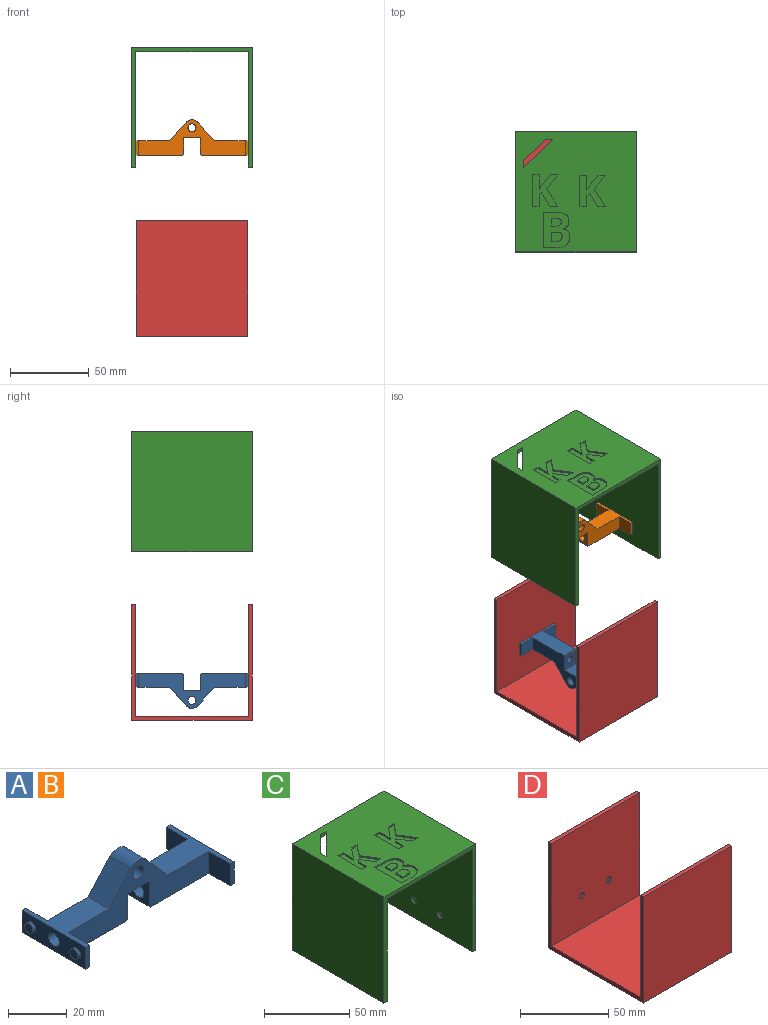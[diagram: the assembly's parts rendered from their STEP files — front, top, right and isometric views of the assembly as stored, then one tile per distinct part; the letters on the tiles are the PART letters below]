
ASSEMBLY  parts=4 mates=3
PART A: 35 faces, bbox 73.5x30.6x22.4 mm
  f0: plane 11.29x10.07mm, normal (0.75,0,0.67), area 151.4mm2, adj f1,f12,f13,f14
  f1: cylinder r=5.08mm len=10.01mm, axis (0,1,0), area 89.4mm2, adj f0,f2,f13,f14
  f2: plane 11.57x10.3mm, normal (-0.75,0,0.67), area 155mm2, adj f1,f3,f13,f14
  f3: plane 30.59x21.47mm, normal (0,0,1), area 252.2mm2, adj f2,f13,f14,f15,f16,f17,f18,f19
  f4: plane 30.59x29.85mm, normal (0,0,-1), area 336.1mm2, adj f5,f13,f14,f15,f16,f17,f18,f19
  f5: plane 10.01x0.64mm, normal (0.71,0,-0.71), area 9mm2, adj f4,f6,f13,f14
  f6: plane 10.3x10.01mm, normal (1,0,0), area 82.6mm2, adj f5,f7,f13,f14,f34
  f7: plane 10.16x10.01mm, normal (0,0,-1), area 101.7mm2, adj f6,f8,f13,f14
  f8: plane 10.3x10.01mm, normal (-1,0,0), area 82.6mm2, adj f7,f9,f13,f14,f33
  f9: plane 10.01x0.64mm, normal (-0.71,0,-0.71), area 9mm2, adj f8,f10,f13,f14
  f10: plane 30.59x29.85mm, normal (0,0,-1), area 336.1mm2, adj f9,f13,f14,f24,f25,f26,f27,f28
  f11: cylinder r=2.55mm len=10.01mm, axis (0,1,0), area 160.5mm2, adj f13,f14
  f12: plane 30.59x21.47mm, normal (0,0,1), area 252.2mm2, adj f0,f13,f14,f24,f25,f26,f27,f28
  f13: plane 67.49x22.39mm, normal (0,-1,0), area 699.3mm2, adj f0,f1,f2,f3,f4,f5,f6,f7
  f14: plane 67.49x22.39mm, normal (0,1,0), area 699.3mm2, adj f0,f1,f2,f3,f4,f5,f6,f7
  f15: plane 10.29x9.12mm, normal (1,0,0), area 93.9mm2, adj f3,f4,f13,f17
  f16: plane 9.12x1.82mm, normal (0,1,0), area 16.6mm2, adj f3,f4,f18,f19
  f17: plane 9.12x1.82mm, normal (0,-1,0), area 16.6mm2, adj f3,f4,f15,f18
  f18: plane 30.59x9.12mm, normal (-1,0,0), area 233.8mm2, adj f3,f4,f16,f17,f20,f22,f34
  f19: plane 10.29x9.12mm, normal (1,0,0), area 93.9mm2, adj f3,f4,f14,f16
  f20: cylinder r=1.98mm len=3.96mm, axis (1,0,0), area 14.9mm2, adj f18,f21
  f21: plane 3.96x3.96mm, normal (-1,0,0), area 12.3mm2, adj f20
  f22: cylinder r=1.98mm len=3.96mm, axis (1,0,0), area 14.9mm2, adj f18,f23
  f23: plane 3.96x3.96mm, normal (-1,0,0), area 12.3mm2, adj f22
  f24: plane 10.29x9.12mm, normal (-1,0,0), area 93.9mm2, adj f10,f12,f14,f25
  f25: plane 9.12x1.82mm, normal (0,1,0), area 16.6mm2, adj f10,f12,f24,f27
  f26: plane 9.12x1.82mm, normal (0,-1,0), area 16.6mm2, adj f10,f12,f27,f28
  f27: plane 30.59x9.12mm, normal (1,0,0), area 233.8mm2, adj f10,f12,f25,f26,f29,f31,f33
  f28: plane 10.29x9.12mm, normal (-1,0,0), area 93.9mm2, adj f10,f12,f13,f26
  f29: cylinder r=1.98mm len=3.96mm, axis (-1,0,0), area 14.9mm2, adj f27,f30
  f30: plane 3.96x3.96mm, normal (1,0,0), area 12.3mm2, adj f29
  f31: cylinder r=1.98mm len=3.96mm, axis (-1,0,0), area 14.9mm2, adj f27,f32
  f32: plane 3.96x3.96mm, normal (1,0,0), area 12.3mm2, adj f31
  f33: cylinder r=2.55mm len=30.48mm, axis (-1,0,0), area 488.9mm2, adj f8,f27
  f34: cylinder r=2.55mm len=30.48mm, axis (-1,0,0), area 488.9mm2, adj f6,f18
PART B: same geometry as A
PART C: 78 faces, bbox 76.2x76.2x76.2 mm
  f0: plane 76.2x76.2mm, normal (0,0,1), area 5029.8mm2, adj f3,f4,f6,f7,f10,f11,f12,f13
  f1: plane 76.2x71.12mm, normal (0,0,-1), area 5348.8mm2, adj f3,f4,f8,f9,f10,f11,f12,f13
  f2: plane 76.2x2.54mm, normal (0,0,-1), area 193.5mm2, adj f3,f4,f7,f9
  f3: plane 76.2x76.2mm, normal (0,-1,0), area 567.7mm2, adj f0,f1,f2,f5,f6,f7,f8,f9
  f4: plane 76.2x76.2mm, normal (0,1,0), area 567.7mm2, adj f0,f1,f2,f5,f6,f7,f8,f9
  f5: plane 76.2x2.54mm, normal (0,0,-1), area 193.5mm2, adj f3,f4,f6,f8
  f6: plane 76.2x76.2mm, normal (1,0,0), area 5806.4mm2, adj f0,f3,f4,f5
  f7: plane 76.2x76.2mm, normal (-1,0,0), area 5806.4mm2, adj f0,f2,f3,f4
  f8: plane 76.2x73.66mm, normal (-1,0,0), area 5586.6mm2, adj f1,f3,f4,f5,f75,f77
  f9: plane 76.2x73.66mm, normal (1,0,0), area 5586.6mm2, adj f1,f2,f3,f4,f71,f73
  f10: plane 4.49x2.54mm, normal (0,-1,0), area 11.4mm2, adj f0,f1,f11,f13
  f11: plane 13.47x13.47mm, normal (0.71,-0.71,0), area 48.4mm2, adj f0,f1,f10,f12
  f12: plane 4.49x2.54mm, normal (1,0,0), area 11.4mm2, adj f0,f1,f11,f13
  f13: plane 17.96x17.96mm, normal (-0.71,0.71,0), area 64.5mm2, adj f0,f1,f10,f12
  f14: plane 11.17x7.04mm, normal (-0.85,-0.53,0), area 13.4mm2, adj f0,f15,f26,f27
  f15: plane 8.87x6.99mm, normal (-0.79,0.62,0), area 11.5mm2, adj f0,f14,f16,f27
  f16: plane 4.72x1.02mm, normal (0,-1,0), area 4.8mm2, adj f0,f15,f17,f27
  f17: plane 6.81x5.43mm, normal (0.78,-0.62,0), area 8.9mm2, adj f0,f16,f18,f27
  f18: plane 2.36x1.67mm, normal (0.82,-0.58,0), area 2.9mm2, adj f0,f17,f19,f27
  f19: plane 9.17x1.02mm, normal (-1,0,0), area 9.3mm2, adj f0,f18,f20,f27
  f20: plane 4.25x1.02mm, normal (0,-1,0), area 4.3mm2, adj f0,f19,f21,f27
  f21: plane 20.04x1.02mm, normal (1,0,0), area 20.4mm2, adj f0,f20,f22,f27
  f22: plane 4.25x1.02mm, normal (0,1,0), area 4.3mm2, adj f0,f21,f23,f27
  f23: plane 7.15x1.02mm, normal (-1,0,0), area 7.3mm2, adj f0,f22,f24,f27
  f24: plane 1.79x1.29mm, normal (-0.58,0.81,0), area 2.2mm2, adj f0,f23,f25,f27
  f25: plane 8.44x5.25mm, normal (0.85,0.53,0), area 10.1mm2, adj f0,f24,f26,f27
  f26: plane 4.82x1.02mm, normal (0,1,0), area 4.9mm2, adj f0,f14,f25,f27
  f27: plane 20.04x16.12mm, normal (0,0,1), area 184.2mm2, adj f14,f15,f16,f17,f18,f19,f20,f21
  f28: plane 11.02x6.95mm, normal (-0.85,-0.53,0), area 13.2mm2, adj f0,f29,f40,f41
  f29: plane 8.75x6.9mm, normal (-0.79,0.62,0), area 11.3mm2, adj f0,f28,f30,f41
  f30: plane 4.65x1.02mm, normal (0,-1,0), area 4.7mm2, adj f0,f29,f31,f41
  f31: plane 6.72x5.36mm, normal (0.78,-0.62,0), area 8.7mm2, adj f0,f30,f32,f41
  f32: plane 2.33x1.65mm, normal (0.82,-0.58,0), area 2.9mm2, adj f0,f31,f33,f41
  f33: plane 9.05x1.02mm, normal (-1,0,0), area 9.2mm2, adj f0,f32,f34,f41
  f34: plane 4.19x1.02mm, normal (0,-1,0), area 4.3mm2, adj f0,f33,f35,f41
  f35: plane 19.76x1.02mm, normal (1,0,0), area 20.1mm2, adj f0,f34,f36,f41
  f36: plane 4.19x1.02mm, normal (0,1,0), area 4.3mm2, adj f0,f35,f37,f41
  f37: plane 7.06x1.02mm, normal (-1,0,0), area 7.2mm2, adj f0,f36,f38,f41
  f38: plane 1.77x1.27mm, normal (-0.58,0.81,0), area 2.2mm2, adj f0,f37,f39,f41
  f39: plane 8.33x5.18mm, normal (0.85,0.53,0), area 10mm2, adj f0,f38,f40,f41
  f40: plane 4.76x1.02mm, normal (0,1,0), area 4.8mm2, adj f0,f28,f39,f41
  f41: plane 19.76x15.9mm, normal (0,0,1), area 179.2mm2, adj f28,f29,f30,f31,f32,f33,f34,f35
  f42: plane 22.51x1.02mm, normal (1,0,0), area 22.9mm2, adj f0,f43,f66,f67
  f43: plane 8.42x1.02mm, normal (0,1,0), area 8.6mm2, adj f0,f42,f44,f67
  f44: extruded ~6.05x1.72mm, area 6.5mm2, adj f0,f43,f45,f67
  f45: extruded ~4.8x2.23mm, area 5.6mm2, adj f0,f44,f46,f67
  f46: extruded ~3.48x1.02mm, area 3.7mm2, adj f0,f45,f47,f67
  f47: extruded ~3.09x1.79mm, area 3.7mm2, adj f0,f46,f48,f67
  f48: plane 1.02x0.15mm, normal (-1,0,0), area 0.2mm2, adj f0,f47,f49,f67
  f49: extruded ~2.52x1.55mm, area 3.1mm2, adj f0,f48,f50,f67
  f50: extruded ~3.31x1.02mm, area 3.6mm2, adj f0,f49,f51,f67
  f51: extruded ~4.33x2.16mm, area 5.2mm2, adj f0,f50,f52,f67
  f52: extruded ~6.95x1.36mm, area 7.3mm2, adj f0,f51,f66,f67
  f53: plane 5.01x1.02mm, normal (-1,0,0), area 5.1mm2, adj f54,f64,f67,f69
  f54: plane 2.51x1.02mm, normal (0,1,0), area 2.5mm2, adj f53,f55,f67,f69
  f55: extruded ~3x1.02mm, area 3.1mm2, adj f54,f56,f67,f69
  f56: extruded ~1.86x1.02mm, area 2.2mm2, adj f55,f57,f67,f69
  f57: extruded ~1.99x1.02mm, area 2.3mm2, adj f56,f58,f67,f69
  f58: extruded ~2.81x1.02mm, area 3mm2, adj f57,f64,f67,f69
  f59: plane 2.96x1.02mm, normal (0,1,0), area 3mm2, adj f60,f65,f67,f68
  f60: extruded ~4x2.8mm, area 5.6mm2, adj f59,f61,f67,f68
  f61: extruded ~2.31x1.02mm, area 2.6mm2, adj f60,f62,f67,f68
  f62: extruded ~2.91x1.02mm, area 3.1mm2, adj f61,f63,f67,f68
  f63: plane 3.11x1.02mm, normal (0,-1,0), area 3.2mm2, adj f62,f65,f67,f68
  f64: plane 2.77x1.02mm, normal (0,-1,0), area 2.8mm2, adj f53,f58,f67,f69
  f65: plane 5.87x1.02mm, normal (-1,0,0), area 6mm2, adj f59,f63,f67,f68
  f66: plane 7.01x1.02mm, normal (0,-1,0), area 7.1mm2, adj f0,f42,f52,f67
  f67: plane 22.51x16.69mm, normal (0,0,1), area 276.3mm2, adj f42,f43,f44,f45,f46,f47,f48,f49
  f68: plane 6.96x5.87mm, normal (0,0,1), area 37mm2, adj f59,f60,f61,f62,f63,f65
  f69: plane 6.45x5.01mm, normal (0,0,1), area 29.4mm2, adj f53,f54,f55,f56,f57,f58,f64
  f70: plane 4.09x4.09mm, normal (1,0,0), area 13.1mm2, adj f71
  f71: cylinder r=2.04mm len=4.09mm, axis (1,0,0), area 16.3mm2, adj f9,f70
  f72: plane 4.09x4.09mm, normal (1,0,0), area 13.1mm2, adj f73
  f73: cylinder r=2.04mm len=4.09mm, axis (1,0,0), area 16.3mm2, adj f9,f72
  f74: plane 4.09x4.09mm, normal (-1,0,0), area 13.1mm2, adj f75
  f75: cylinder r=2.04mm len=4.09mm, axis (1,0,0), area 16.3mm2, adj f8,f74
  f76: plane 4.09x4.09mm, normal (-1,0,0), area 13.1mm2, adj f77
  f77: cylinder r=2.04mm len=4.09mm, axis (1,0,0), area 16.3mm2, adj f8,f76
PART D: 18 faces, bbox 70.6x76.2x73.4 mm
  f0: plane 70.87x70.61mm, normal (0,-1,0), area 4977.7mm2, adj f2,f3,f4,f5,f15,f17
  f1: plane 70.87x70.61mm, normal (0,1,0), area 4977.7mm2, adj f2,f3,f4,f6,f11,f13
  f2: plane 71.12x70.61mm, normal (0,0,1), area 5021.9mm2, adj f0,f1,f3,f4
  f3: plane 76.2x73.41mm, normal (1,0,0), area 553.5mm2, adj f0,f1,f2,f5,f6,f7,f8,f9
  f4: plane 76.2x73.41mm, normal (-1,0,0), area 553.5mm2, adj f0,f1,f2,f5,f6,f7,f8,f9
  f5: plane 70.61x2.54mm, normal (0,0,1), area 179.4mm2, adj f0,f3,f4,f8
  f6: plane 70.61x2.54mm, normal (0,0,1), area 179.4mm2, adj f1,f3,f4,f7
  f7: plane 73.41x70.61mm, normal (0,-1,0), area 5183.3mm2, adj f3,f4,f6,f9
  f8: plane 73.41x70.61mm, normal (0,1,0), area 5183.3mm2, adj f3,f4,f5,f9
  f9: plane 76.2x70.61mm, normal (0,0,-1), area 5380.6mm2, adj f3,f4,f7,f8
  f10: plane 4.09x4.09mm, normal (0,1,0), area 13.1mm2, adj f11
  f11: cylinder r=2.04mm len=4.09mm, axis (0,1,0), area 16.3mm2, adj f1,f10
  f12: plane 4.09x4.09mm, normal (0,1,0), area 13.1mm2, adj f13
  f13: cylinder r=2.04mm len=4.09mm, axis (0,1,0), area 16.3mm2, adj f1,f12
  f14: plane 4.09x4.09mm, normal (0,-1,0), area 13.1mm2, adj f15
  f15: cylinder r=2.04mm len=4.09mm, axis (0,1,0), area 16.3mm2, adj f0,f14
  f16: plane 4.09x4.09mm, normal (0,-1,0), area 13.1mm2, adj f17
  f17: cylinder r=2.04mm len=4.09mm, axis (0,1,0), area 16.3mm2, adj f0,f16
PLACE A rot(axis=(0.71,-0.71,0),180deg) t=(-5,0,12.65)mm
PLACE B t=(0,5,132.16)mm
PLACE C t=(0,38.1,144.86)mm
PLACE D t=(0,38.1,38.1)mm
MATE fastened A.f20 <-> D.f13  axis (0,1,0) through (-10.79,36.75,25.4)mm
MATE slider A.f7 <-> B.f7  axis (0,0,1) through (0,0,19.02)mm
MATE fastened B.f31 <-> C.f73  axis (1,0,0) through (36.76,-10.8,119.41)mm
